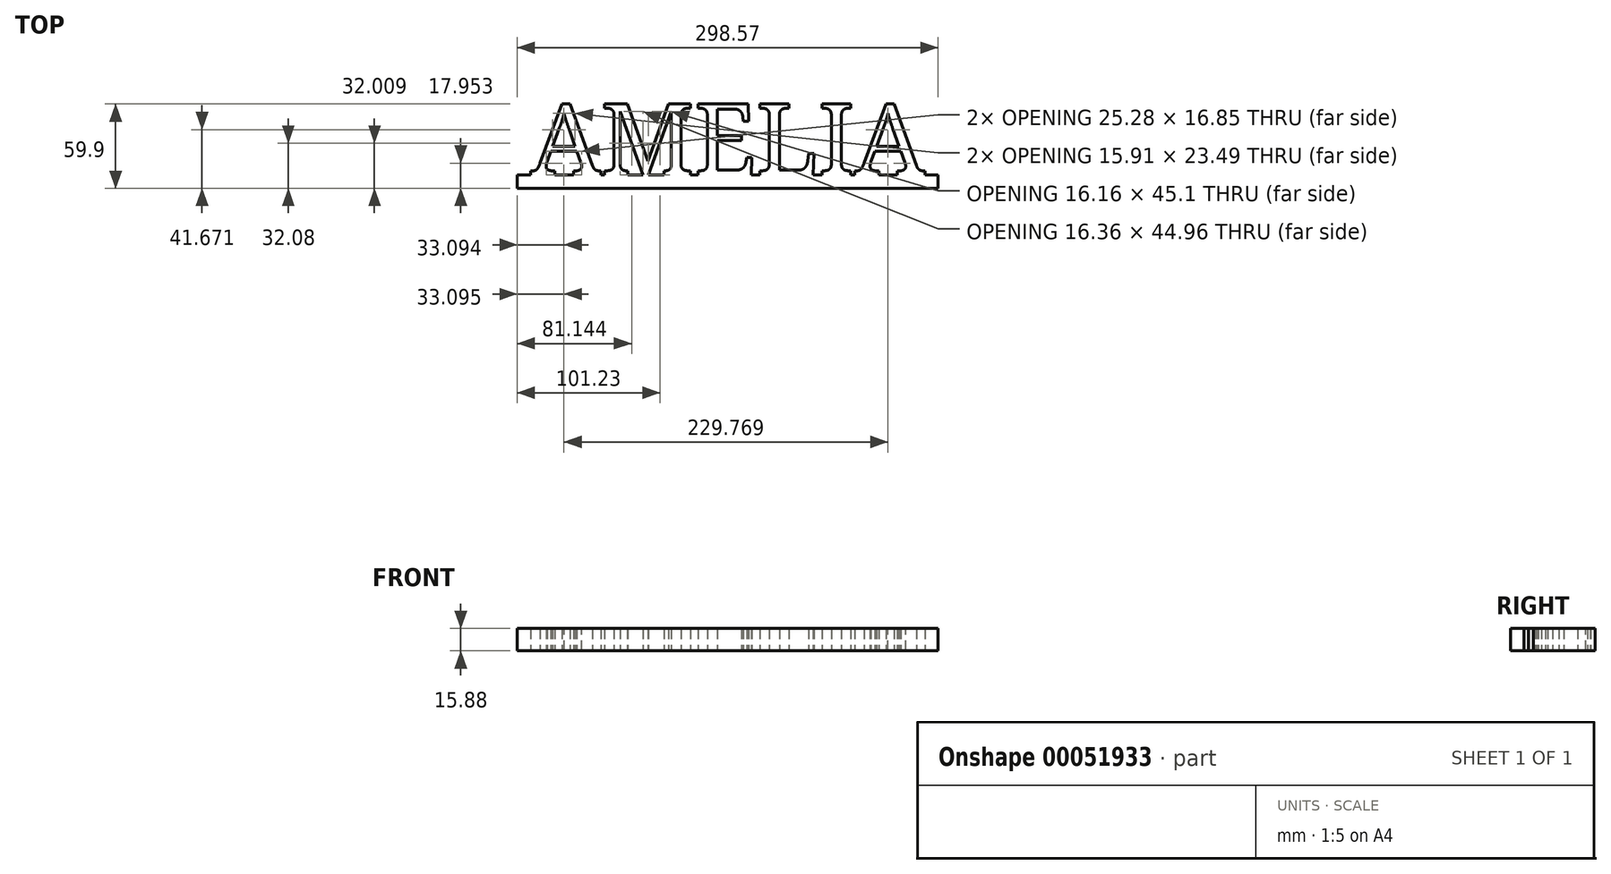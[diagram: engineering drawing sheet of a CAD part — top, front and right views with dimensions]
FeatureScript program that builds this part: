
annotation { "Feature Type Name" : "Feature", "Feature Type Description" : "" }
export const myFeature = defineFeature(function(context is Context, id is Id, definition is map)
    precondition{}
    {
        {
            var Q0;
            Q0=qCreatedBy(makeId("Top.planeOp"),FACE);
            var sketch = newSketch(context, id + "F0", { "sketchPlane" : qUnion([Q0])});
            skText(sketch, "E0", { "text": "AMELIA", "fontName": "NotoSerif-Regular.ttf"});
            skLineSegment(sketch, "E1.bottom", {"start": v(-93.6, -38.1) * mm, "end": v(204.96, -38.1) * mm});
            skLineSegment(sketch, "E1.top", {"start": v(-93.6, -47.62) * mm, "end": v(204.96, -47.62) * mm});
            skLineSegment(sketch, "E1.left", {"start": v(-93.6, -38.1) * mm, "end": v(-93.6, -47.62) * mm});
            skLineSegment(sketch, "E1.right", {"start": v(204.96, -38.1) * mm, "end": v(204.96, -47.62) * mm});
            const initialGuessF0  = {"E0": [-0.08408, -0.0381, 1, 0, 0.0508]};
            skSetInitialGuess(sketch, initialGuessF0);
            skSolve(sketch);
        }
        {
            var Q0;
            Q0 = qSketchRegion(id + "F0", true);
            extrude(context, id + "F1", {"entities" : qUnion([Q0]), "depth" : 15.88 * mm});
        }
    });
